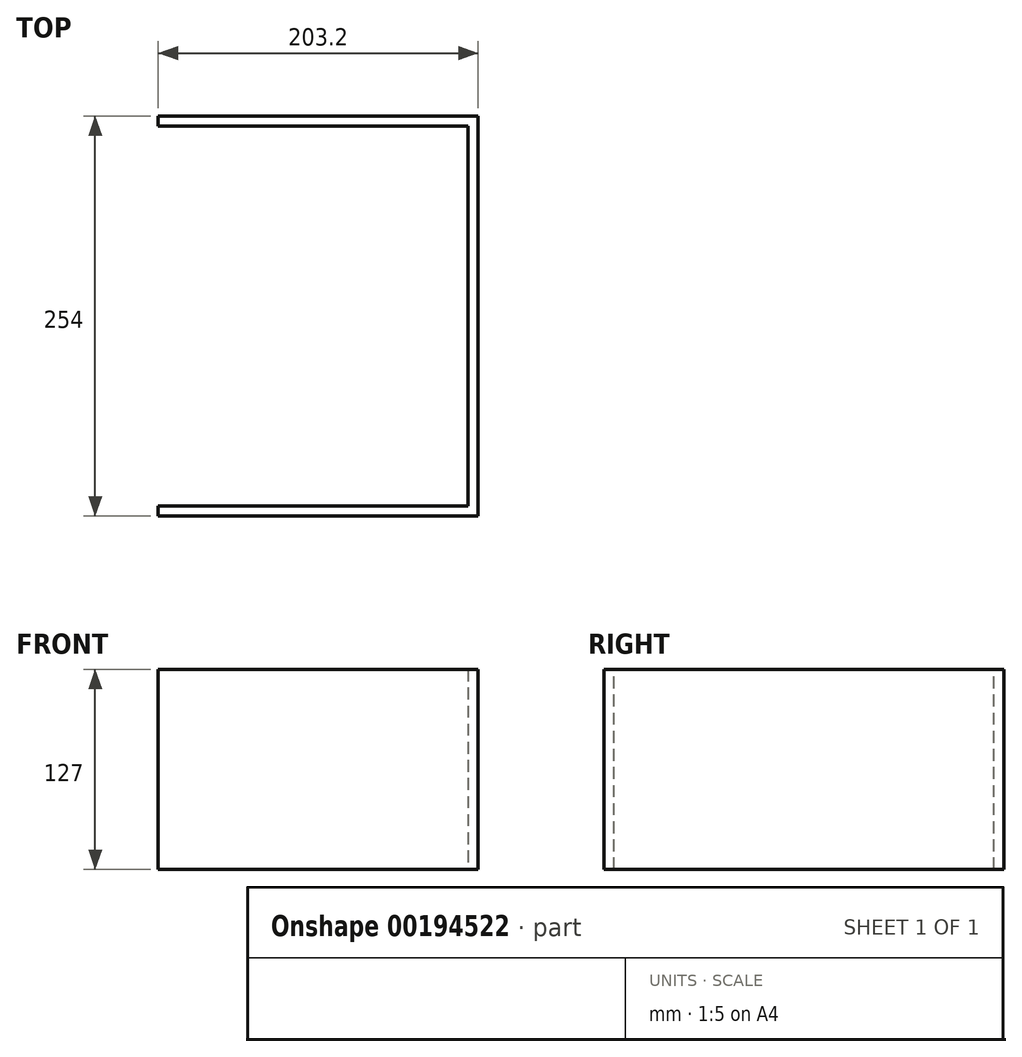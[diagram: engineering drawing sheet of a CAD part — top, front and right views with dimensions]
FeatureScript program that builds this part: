
annotation { "Feature Type Name" : "Feature", "Feature Type Description" : "" }
export const myFeature = defineFeature(function(context is Context, id is Id, definition is map)
    precondition{}
    {
        {
            var Q0;
            Q0=qCreatedBy(makeId("Top.planeOp"),FACE);
            var sketch = newSketch(context, id + "F0", { "sketchPlane" : qUnion([Q0])});
            skLineSegment(sketch, "E0.bottom", {"start": v(114.72, 149.17) * mm, "end": v(-114.72, 149.17) * mm});
            skLineSegment(sketch, "E0.top", {"start": v(114.72, -149.17) * mm, "end": v(-114.72, -149.17) * mm});
            skLineSegment(sketch, "E0.left", {"start": v(114.72, 149.17) * mm, "end": v(114.72, -149.17) * mm});
            skLineSegment(sketch, "E0.right", {"start": v(-114.72, 149.17) * mm, "end": v(-114.72, -149.17) * mm});
            skPoint(sketch, "E0.middle", {"position": v(0, 0) * mm});
            skSolve(sketch);
        }
        {
            var Q0;
            Q0=qCreatedBy(makeId("Front.planeOp"),FACE);
            var sketch = newSketch(context, id + "F1", { "sketchPlane" : qUnion([Q0])});
            skLineSegment(sketch, "E1.bottom", {"start": v(101.6, 127) * mm, "end": v(-101.6, 127) * mm});
            skLineSegment(sketch, "E1.top", {"start": v(101.6, -127) * mm, "end": v(-101.6, -127) * mm});
            skLineSegment(sketch, "E1.left", {"start": v(101.6, 127) * mm, "end": v(101.6, -127) * mm});
            skLineSegment(sketch, "E1.right", {"start": v(-101.6, 127) * mm, "end": v(-101.6, -127) * mm});
            skPoint(sketch, "E1.middle", {"position": v(0, 0) * mm});
            skSolve(sketch);
        }
        {
            var Q0;
            Q0=qCreatedBy(makeId("Front.planeOp"),FACE);
            cPlane(context, id + "F2", {"entities" : qUnion([Q0]), "cplaneType" : CPlaneType.OFFSET, "offset" : 127 * mm, "width" : 152.4 * mm, "height" : 152.4 * mm});
        }
        {
            var Q0;
            Q0=qCreatedBy(id+"F2.planeOp",FACE);
            var sketch = newSketch(context, id + "F3", { "sketchPlane" : qUnion([Q0])});
            skLineSegment(sketch, "E2.0", {"start": v(101.6, 127) * mm, "end": v(-101.6, 127) * mm});
            skLineSegment(sketch, "E3.0", {"start": v(-101.6, 127) * mm, "end": v(-101.6, -127) * mm});
            skLineSegment(sketch, "E4.0", {"start": v(101.6, -127) * mm, "end": v(-101.6, -127) * mm});
            skLineSegment(sketch, "E5.0", {"start": v(101.6, 127) * mm, "end": v(101.6, -127) * mm});
            skSolve(sketch);
        }
        {
            var Q0;
            Q0=makeQuery(id+"F1.imprint","IMPRINT",FACE,{"disambiguationData":[TD([[makeQuery(id+"F1.imprint","IMPRINT",EDGE,{"derivedFrom":sQuery(id+"F1.wireOp",EDGE,"E1.bottom")}),1.0]])]});
            cPlane(context, id + "F4", {"entities" : qUnion([Q0]), "cplaneType" : CPlaneType.OFFSET, "offset" : 127 * mm, "oppositeDirection" : true, "width" : 152.4 * mm, "height" : 152.4 * mm});
        }
        {
            var Q0;
            Q0=qCreatedBy(id+"F4.planeOp",FACE);
            var sketch = newSketch(context, id + "F5", { "sketchPlane" : qUnion([Q0])});
            skLineSegment(sketch, "E6.0", {"start": v(101.6, 127) * mm, "end": v(-101.6, 127) * mm});
            skLineSegment(sketch, "E7.0", {"start": v(-101.6, 127) * mm, "end": v(-101.6, -127) * mm});
            skLineSegment(sketch, "E8.0", {"start": v(101.6, 127) * mm, "end": v(101.6, -127) * mm});
            skLineSegment(sketch, "E9.0", {"start": v(101.6, -127) * mm, "end": v(-101.6, -127) * mm});
            skSolve(sketch);
        }
        {
            var Q0;
            Q0=makeQuery(id+"F0.imprint","IMPRINT",FACE,{"disambiguationData":[TD([[makeQuery(id+"F0.imprint","IMPRINT",EDGE,{"derivedFrom":sQuery(id+"F0.wireOp",EDGE,"E0.bottom")}),1.0]])]});
            cPlane(context, id + "F6", {"entities" : qUnion([Q0]), "cplaneType" : CPlaneType.OFFSET, "offset" : 127 * mm, "width" : 152.4 * mm, "height" : 152.4 * mm});
        }
        {
            var Q0;
            Q0=qCreatedBy(id+"F6.planeOp",FACE);
            var sketch = newSketch(context, id + "F7", { "sketchPlane" : qUnion([Q0])});
            skLineSegment(sketch, "E10.0", {"start": v(101.6, -127) * mm, "end": v(-101.6, -127) * mm});
            skLineSegment(sketch, "E11.0", {"start": v(101.6, 127) * mm, "end": v(-101.6, 127) * mm});
            skLineSegment(sketch, "E12", {"start": v(-101.6, -127) * mm, "end": v(-101.6, 127) * mm});
            skLineSegment(sketch, "E13", {"start": v(101.6, -127) * mm, "end": v(101.6, 127) * mm});
            skSolve(sketch);
        }
        {
            var Q0;
            Q0=makeQuery(id+"F7.imprint","IMPRINT",FACE,{"disambiguationData":[TD([[makeQuery(id+"F7.imprint","IMPRINT",EDGE,{"derivedFrom":sQuery(id+"F7.wireOp",EDGE,"E10.0")}),-1.0]])]});
            extrude(context, id + "F8", {"entities" : qUnion([Q0]), "depth" : 127 * mm});
        }
        {
            var Q0;
            Q0=makeQuery(id+"F8.opExtrude","CAP_FACE",FACE,{"disambiguationData":[OSD([sQuery(id+"F7.wireOp",EDGE,"E10.0"),sQuery(id+"F7.wireOp",EDGE,"E11.0"),sQuery(id+"F7.wireOp",EDGE,"E12"),sQuery(id+"F7.wireOp",EDGE,"E13")])],"isStart":false});
            var Q1;
            Q1=makeQuery(id+"F8.opExtrude","CAP_FACE",FACE,{"disambiguationData":[OSD([sQuery(id+"F7.wireOp",EDGE,"E10.0"),sQuery(id+"F7.wireOp",EDGE,"E11.0"),sQuery(id+"F7.wireOp",EDGE,"E12"),sQuery(id+"F7.wireOp",EDGE,"E13")])],"isStart":true});
            shell(context, id + "F9", {"entities" : qUnion([Q0, Q1]), "thickness" : 6.35 * mm});
        }
        {
            var Q0;
            Q0=makeQuery(id+"F9.opShell","OFFSET_FACE",FACE,{"disambiguationData":[OSD([sQuery(id+"F7.wireOp",EDGE,"E12")])]});
            extrude(context, id + "F10", {"entities" : qUnion([Q0]), "operationType" : NewBodyOperationType.REMOVE, "oppositeDirection" : true, "depth" : 25.4 * mm});
        }
    });
